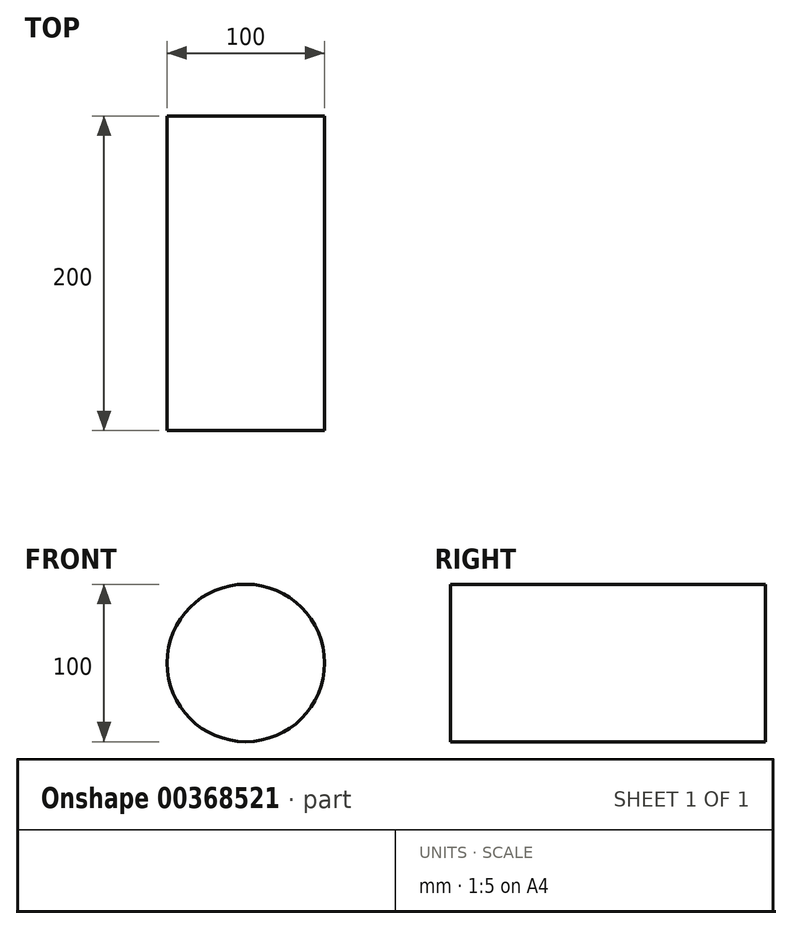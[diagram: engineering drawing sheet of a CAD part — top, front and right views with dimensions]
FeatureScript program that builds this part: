
annotation { "Feature Type Name" : "Feature", "Feature Type Description" : "" }
export const myFeature = defineFeature(function(context is Context, id is Id, definition is map)
    precondition{}
    {
        {
            var Q0;
            Q0=qCreatedBy(makeId("Front.planeOp"),FACE);
            var sketch = newSketch(context, id + "F0", { "sketchPlane" : qUnion([Q0])});
            skCircle(sketch, "E0", {"center": v(0, 0) * mm, "radius": 50 * mm});
            skSolve(sketch);
        }
        {
            var Q0;
            Q0=makeQuery(id+"F0.imprint","IMPRINT",FACE,{"disambiguationData":[TD([[makeQuery(id+"F0.imprint","IMPRINT",EDGE,{"derivedFrom":sQuery(id+"F0.wireOp",EDGE,"E0")}),1.0]])]});
            extrude(context, id + "F1", {"entities" : qUnion([Q0]), "depth" : 200 * mm});
        }
    });
